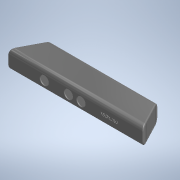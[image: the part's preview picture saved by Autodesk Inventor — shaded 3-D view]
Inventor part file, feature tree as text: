
AUTODESK INVENTOR PART (.ipt)
format: ipt  version: 2020 (Build 240168000, 168)  size: 483,328 bytes
history: mixed  units: mm (DEFAULTED — no unit token found)
features: extrude x1, sketch x1, fillet x1, imported_body x1
ambient origin geometry x8: Origin, YZ Plane, XZ Plane, XY Plane, X Axis, Y Axis, Z Axis, Center Point
bodies: Solid1 (imported_parasolid)
feature tree (4):
  extrude  "Extrusion1"  Depth=0.5mm
  sketch  "Sketch1"  dims[d0=26.75mm d1=0.0mm d2=0.5mm d3=0.872665mm]
  fillet  "Fillet3"  Radius=0.872665mm
  imported_body  NMx_Import_Brep_tag  [imported B-rep: ~5 faces, bbox_mm=[0.0, 0.0, 0.0]]
